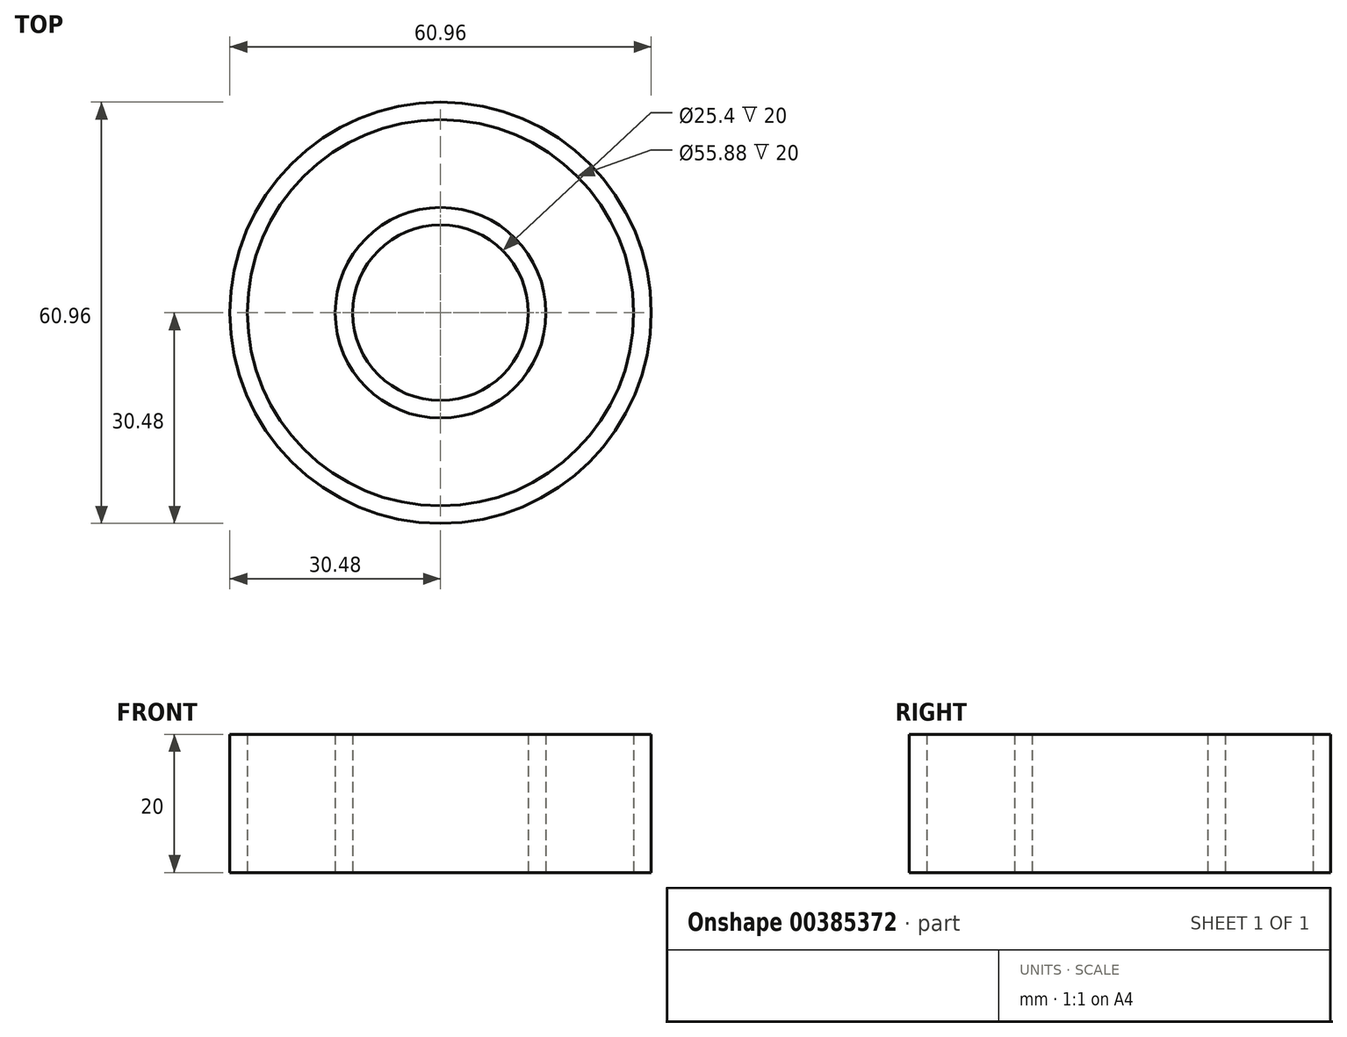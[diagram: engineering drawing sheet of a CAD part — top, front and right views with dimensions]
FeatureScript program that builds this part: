
annotation { "Feature Type Name" : "Feature", "Feature Type Description" : "" }
export const myFeature = defineFeature(function(context is Context, id is Id, definition is map)
    precondition{}
    {
        {
            var Q0;
            Q0=qCreatedBy(makeId("Top.planeOp"),FACE);
            var sketch = newSketch(context, id + "F0", { "sketchPlane" : qUnion([Q0])});
            skCircle(sketch, "E0", {"center": v(0, 0) * mm, "radius": 12.7 * mm});
            skCircle(sketch, "E1", {"center": v(0, 0) * mm, "radius": 15.24 * mm});
            skCircle(sketch, "E2", {"center": v(0, 0) * mm, "radius": 27.94 * mm});
            skCircle(sketch, "E3", {"center": v(0, 0) * mm, "radius": 30.48 * mm});
            skSolve(sketch);
        }
        {
            var Q0;
            Q0=makeQuery(id+"F0.imprint","IMPRINT",FACE,{"disambiguationData":[TD([[makeQuery(id+"F0.imprint","IMPRINT",EDGE,{"derivedFrom":sQuery(id+"F0.wireOp",EDGE,"E2")}),-1.0]])]});
            var Q1;
            Q1=makeQuery(id+"F0.imprint","IMPRINT",FACE,{"disambiguationData":[TD([[makeQuery(id+"F0.imprint","IMPRINT",EDGE,{"derivedFrom":sQuery(id+"F0.wireOp",EDGE,"E0")}),-1.0]])]});
            extrude(context, id + "F1", {"entities" : qUnion([Q0, Q1]), "depth" : 20 * mm});
        }
    });
